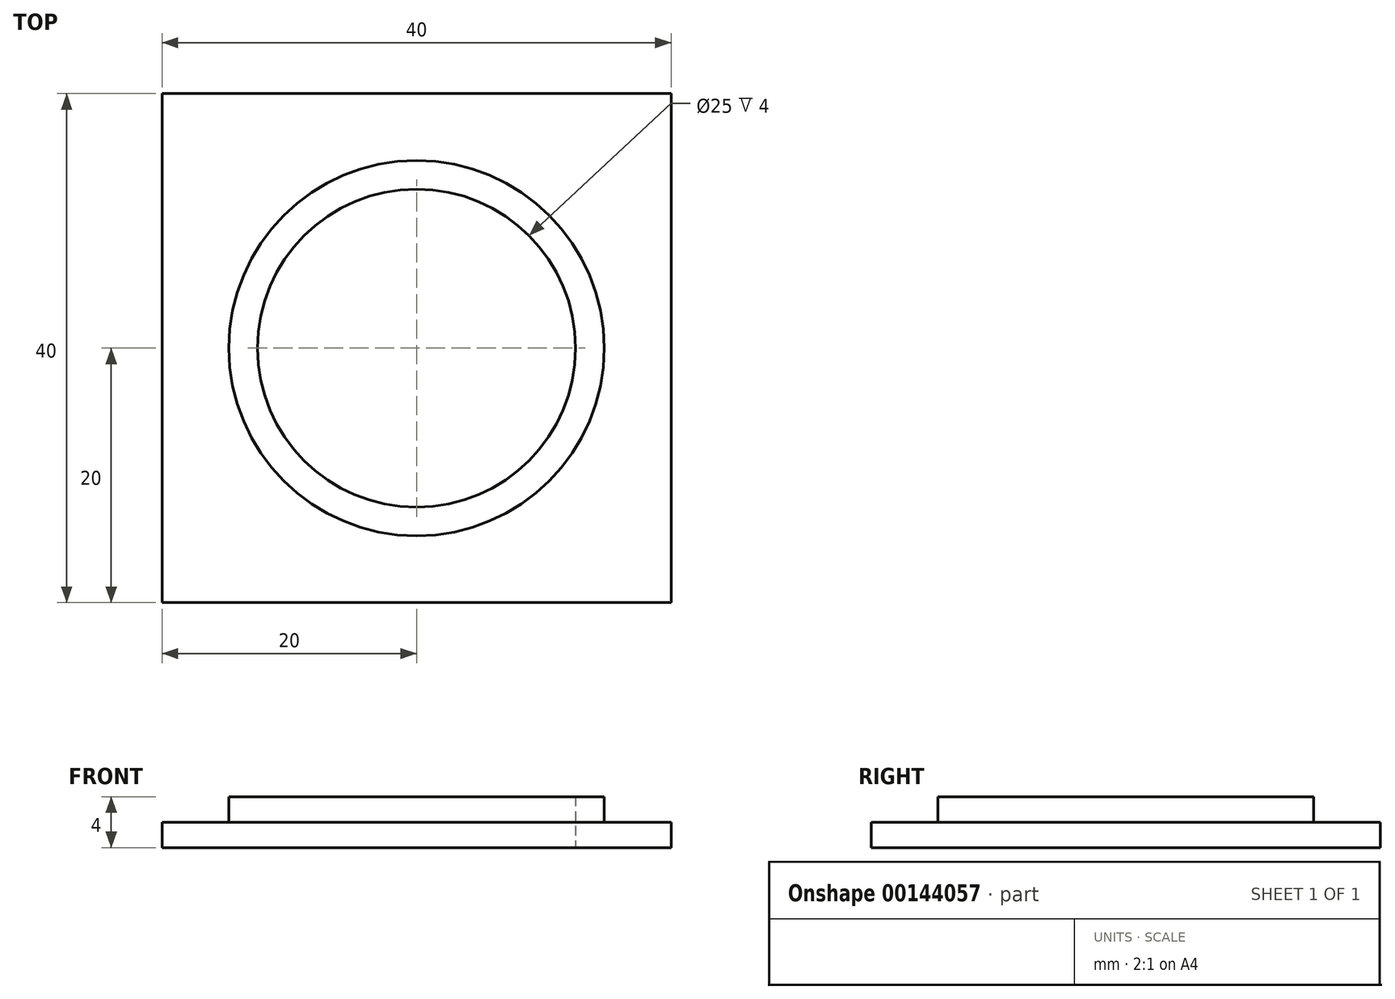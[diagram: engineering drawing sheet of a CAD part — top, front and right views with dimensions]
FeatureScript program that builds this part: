
annotation { "Feature Type Name" : "Feature", "Feature Type Description" : "" }
export const myFeature = defineFeature(function(context is Context, id is Id, definition is map)
    precondition{}
    {
        {
            var Q0;
            Q0=qCreatedBy(makeId("Top.planeOp"),FACE);
            var sketch = newSketch(context, id + "F0", { "sketchPlane" : qUnion([Q0])});
            skCircle(sketch, "E0", {"center": v(0, 0) * mm, "radius": 12.5 * mm});
            skLineSegment(sketch, "E1.bottom", {"start": v(20, 20) * mm, "end": v(-20, 20) * mm});
            skLineSegment(sketch, "E1.top", {"start": v(20, -20) * mm, "end": v(-20, -20) * mm});
            skLineSegment(sketch, "E1.left", {"start": v(20, 20) * mm, "end": v(20, -20) * mm});
            skLineSegment(sketch, "E1.right", {"start": v(-20, 20) * mm, "end": v(-20, -20) * mm});
            skSolve(sketch);
        }
        {
            var Q0;
            Q0=makeQuery(id+"F0.imprint","IMPRINT",FACE,{"disambiguationData":[TD([[makeQuery(id+"F0.imprint","IMPRINT",EDGE,{"derivedFrom":sQuery(id+"F0.wireOp",EDGE,"E0")}),-1.0]])]});
            extrude(context, id + "F1", {"entities" : qUnion([Q0]), "depth" : 2 * mm});
        }
        {
            var Q0;
            Q0=makeQuery(id+"F1.opExtrude","CAP_FACE",FACE,{"disambiguationData":[OSD([sQuery(id+"F0.wireOp",EDGE,"E0"),sQuery(id+"F0.wireOp",EDGE,"E1.bottom"),sQuery(id+"F0.wireOp",EDGE,"E1.top"),sQuery(id+"F0.wireOp",EDGE,"E1.left"),sQuery(id+"F0.wireOp",EDGE,"E1.right")])],"isStart":false});
            var sketch = newSketch(context, id + "F2", { "sketchPlane" : qUnion([Q0])});
            skCircle(sketch, "E2", {"center": v(0, 0) * mm, "radius": 12.5 * mm});
            skCircle(sketch, "E3", {"center": v(0, 0) * mm, "radius": 14.75 * mm});
            skSolve(sketch);
        }
        {
            var Q0;
            Q0=makeQuery(id+"F2.imprint","IMPRINT",FACE,{"disambiguationData":[TD([[makeQuery(id+"F2.imprint","IMPRINT",EDGE,{"derivedFrom":sQuery(id+"F2.wireOp",EDGE,"E2")}),-1.0]])]});
            extrude(context, id + "F3", {"entities" : qUnion([Q0]), "operationType" : NewBodyOperationType.ADD, "depth" : 2 * mm});
        }
    });
